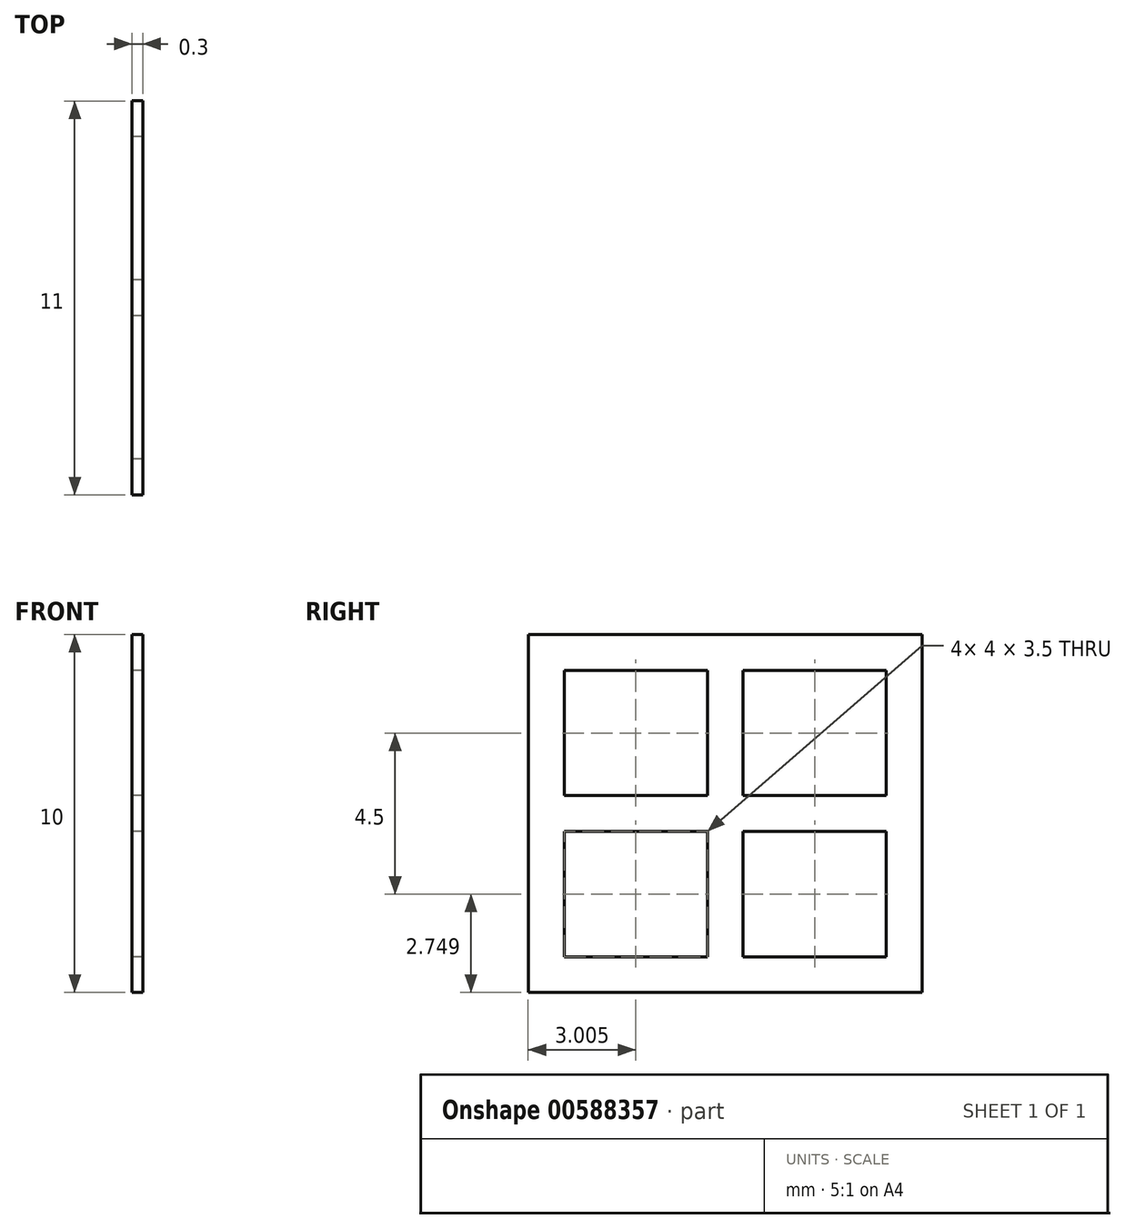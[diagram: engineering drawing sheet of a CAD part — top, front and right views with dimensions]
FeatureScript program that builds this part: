
annotation { "Feature Type Name" : "Feature", "Feature Type Description" : "" }
export const myFeature = defineFeature(function(context is Context, id is Id, definition is map)
    precondition{}
    {
        {
            var Q0;
            Q0=qCreatedBy(makeId("Right.planeOp"),FACE);
            var sketch = newSketch(context, id + "F0", { "sketchPlane" : qUnion([Q0])});
            skCircle(sketch, "E0", {"center": v(-108.18, 18.63) * mm, "radius": 3 * mm});
            skLineSegment(sketch, "E1.bottom", {"start": v(-80.18, 25.63) * mm, "end": v(-69.18, 25.63) * mm});
            skLineSegment(sketch, "E1.top", {"start": v(-80.18, 15.63) * mm, "end": v(-69.18, 15.63) * mm});
            skLineSegment(sketch, "E1.left", {"start": v(-80.18, 25.63) * mm, "end": v(-80.18, 15.63) * mm});
            skLineSegment(sketch, "E1.right", {"start": v(-69.18, 25.63) * mm, "end": v(-69.18, 15.63) * mm});
            skLineSegment(sketch, "E2.bottom", {"start": v(-80.18, 25.63) * mm, "end": v(-75.18, 25.63) * mm});
            skLineSegment(sketch, "E2.top", {"start": v(-79.18, 21.13) * mm, "end": v(-75.18, 21.13) * mm});
            skLineSegment(sketch, "E2.left", {"start": v(-80.18, 25.63) * mm, "end": v(-80.18, 21.13) * mm});
            skLineSegment(sketch, "E2.right", {"start": v(-75.18, 24.63) * mm, "end": v(-75.18, 21.13) * mm});
            skLineSegment(sketch, "E3.bottom", {"start": v(-69.18, 25.63) * mm, "end": v(-74.18, 25.63) * mm});
            skLineSegment(sketch, "E3.top", {"start": v(-70.18, 21.13) * mm, "end": v(-74.18, 21.13) * mm});
            skLineSegment(sketch, "E3.left", {"start": v(-69.18, 25.63) * mm, "end": v(-69.18, 21.13) * mm});
            skLineSegment(sketch, "E3.right", {"start": v(-74.18, 24.63) * mm, "end": v(-74.18, 21.13) * mm});
            skLineSegment(sketch, "E4.bottom", {"start": v(-80.18, 15.63) * mm, "end": v(-75.18, 15.63) * mm});
            skLineSegment(sketch, "E4.top", {"start": v(-79.18, 20.13) * mm, "end": v(-75.18, 20.13) * mm});
            skLineSegment(sketch, "E4.left", {"start": v(-80.18, 15.63) * mm, "end": v(-80.18, 20.13) * mm});
            skLineSegment(sketch, "E4.right", {"start": v(-75.18, 15.63) * mm, "end": v(-75.18, 20.13) * mm});
            skLineSegment(sketch, "E5.bottom", {"start": v(-69.18, 15.63) * mm, "end": v(-74.18, 15.63) * mm});
            skLineSegment(sketch, "E5.top", {"start": v(-70.18, 20.13) * mm, "end": v(-74.18, 20.13) * mm});
            skLineSegment(sketch, "E5.left", {"start": v(-69.18, 15.63) * mm, "end": v(-69.18, 20.13) * mm});
            skLineSegment(sketch, "E5.right", {"start": v(-74.18, 15.63) * mm, "end": v(-74.18, 20.13) * mm});
            skLineSegment(sketch, "E6.bottom", {"start": v(-75.18, 21.13) * mm, "end": v(-79.18, 21.13) * mm});
            skLineSegment(sketch, "E6.top", {"start": v(-75.18, 24.63) * mm, "end": v(-79.18, 24.63) * mm});
            skLineSegment(sketch, "E6.left", {"start": v(-75.18, 21.13) * mm, "end": v(-75.18, 24.63) * mm});
            skLineSegment(sketch, "E6.right", {"start": v(-79.18, 21.13) * mm, "end": v(-79.18, 24.63) * mm});
            skLineSegment(sketch, "E7.bottom", {"start": v(-74.18, 21.13) * mm, "end": v(-70.18, 21.13) * mm});
            skLineSegment(sketch, "E7.top", {"start": v(-74.18, 24.63) * mm, "end": v(-70.18, 24.63) * mm});
            skLineSegment(sketch, "E7.left", {"start": v(-74.18, 21.13) * mm, "end": v(-74.18, 24.63) * mm});
            skLineSegment(sketch, "E7.right", {"start": v(-70.18, 21.13) * mm, "end": v(-70.18, 24.63) * mm});
            skLineSegment(sketch, "E8.bottom", {"start": v(-75.18, 20.13) * mm, "end": v(-79.18, 20.13) * mm});
            skLineSegment(sketch, "E8.top", {"start": v(-75.18, 16.63) * mm, "end": v(-79.18, 16.63) * mm});
            skLineSegment(sketch, "E8.left", {"start": v(-75.18, 20.13) * mm, "end": v(-75.18, 16.63) * mm});
            skLineSegment(sketch, "E8.right", {"start": v(-79.18, 20.13) * mm, "end": v(-79.18, 16.63) * mm});
            skLineSegment(sketch, "E9.bottom", {"start": v(-74.18, 20.13) * mm, "end": v(-70.18, 20.13) * mm});
            skLineSegment(sketch, "E9.top", {"start": v(-74.18, 16.63) * mm, "end": v(-70.18, 16.63) * mm});
            skLineSegment(sketch, "E9.left", {"start": v(-74.18, 20.13) * mm, "end": v(-74.18, 16.63) * mm});
            skLineSegment(sketch, "E9.right", {"start": v(-70.18, 20.13) * mm, "end": v(-70.18, 16.63) * mm});
            skSolve(sketch);
        }
        {
            var Q0;
            Q0=makeQuery(id+"F0.imprint","IMPRINT",FACE,{"disambiguationData":[TD([[makeQuery(id+"F0.imprint","IMPRINT",EDGE,{"derivedFrom":sQuery(id+"F0.wireOp",EDGE,"E1.bottom")}),-1.0]])]});
            extrude(context, id + "F1", {"entities" : qUnion([Q0]), "depth" : .3 * mm, "offsetDistance" : 25 * mm});
        }
    });
